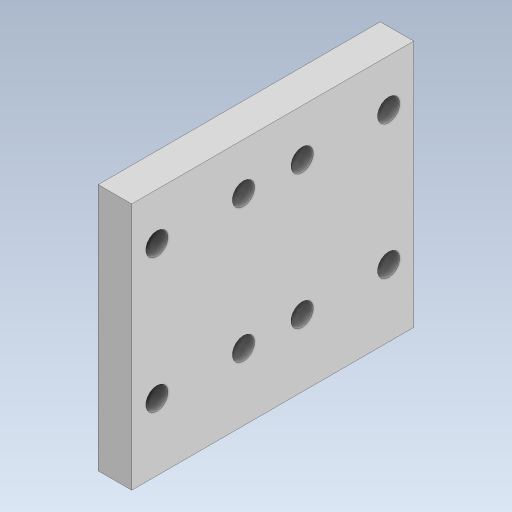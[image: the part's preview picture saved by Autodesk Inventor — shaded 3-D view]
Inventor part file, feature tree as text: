
AUTODESK INVENTOR PART (.ipt)
format: ipt  version: 2023.5 (Build 275446000, 446)  size: 122,368 bytes
history: native  units: in
note: dims shown in document units (in); Inventor stores cm internally (conversion verified against a paired STEP export)
features: extrude x2, sketch x1
ambient origin geometry x8: Origin, YZ Plane, XZ Plane, XY Plane, X Axis, Y Axis, Z Axis, Center Point
bodies: Solid1 (feature_tree)
feature tree (3):
  sketch  "Sketch1"  dims[d0=0.874in d1=0.9941in d2=0.0787in d3=0.2362in d4=0.0886in d5=0.0787in d6=0.3937in d9=0.0787in d10=0.1654in d12=0.1181in d13=0.0in d14=0.0787in d15=0.0787in d16=0.1181in d17=0.0in]
  extrude  "Extrusion1"  Depth=0.9941in
  extrude  "Extrusion2"  Depth=0.1181in
